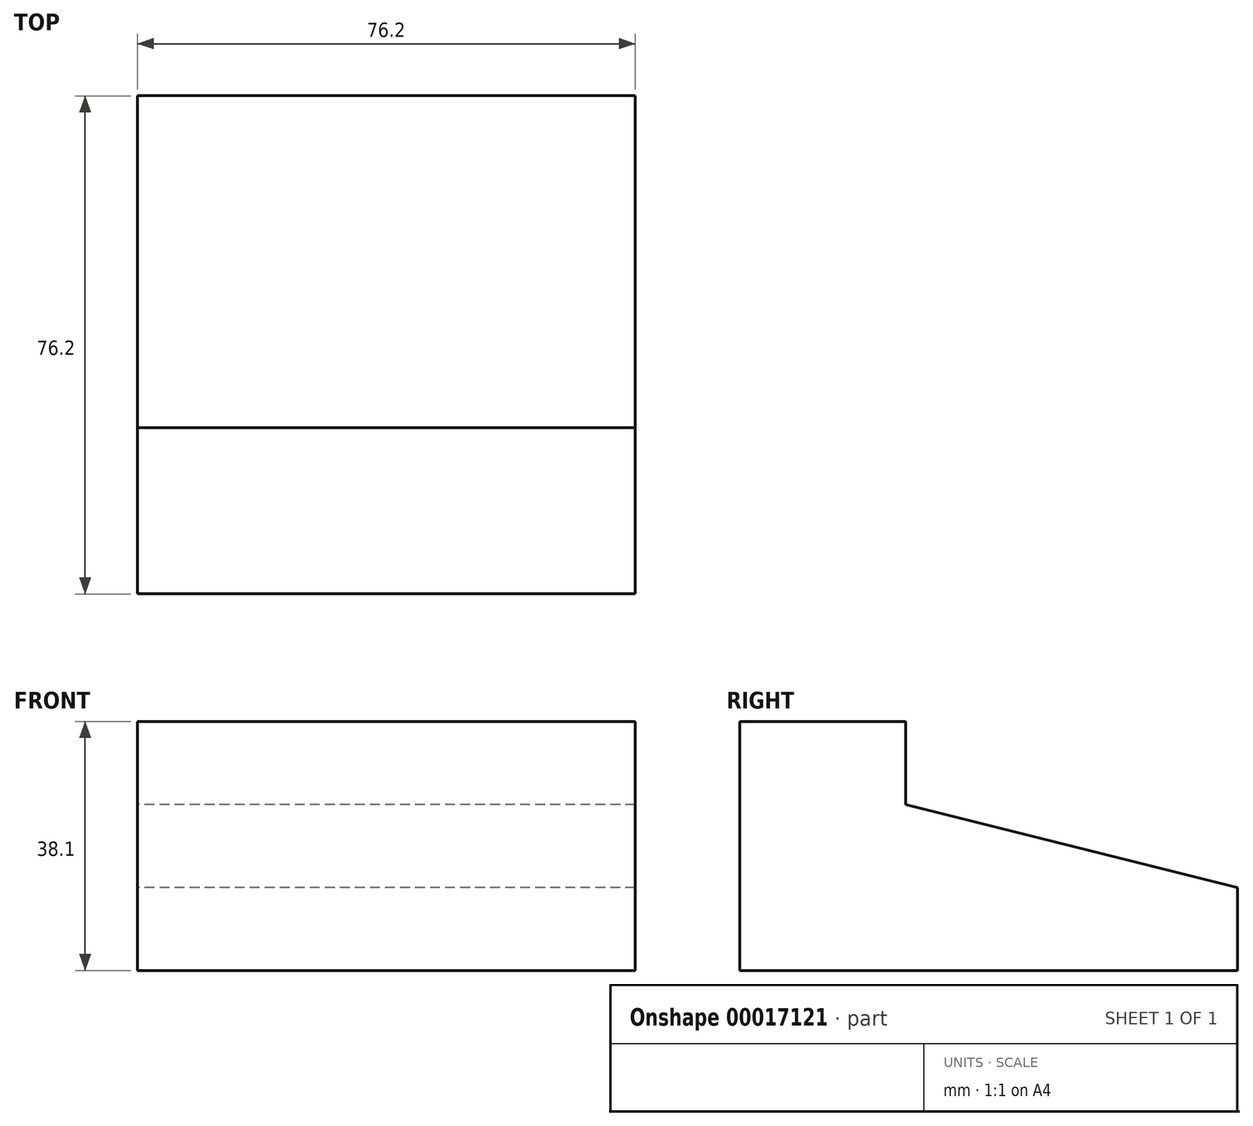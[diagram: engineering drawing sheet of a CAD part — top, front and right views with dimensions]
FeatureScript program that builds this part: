
annotation { "Feature Type Name" : "Feature", "Feature Type Description" : "" }
export const myFeature = defineFeature(function(context is Context, id is Id, definition is map)
    precondition{}
    {
        {
            var Q0;
            Q0=qCreatedBy(makeId("Right.planeOp"),FACE);
            var sketch = newSketch(context, id + "F0", { "sketchPlane" : qUnion([Q0])});
            skLineSegment(sketch, "E0", {"start": v(-41.72, 32.47) * mm, "end": v(-16.32, 32.47) * mm});
            skLineSegment(sketch, "E1", {"start": v(-16.32, 32.47) * mm, "end": v(-16.32, 19.77) * mm});
            skLineSegment(sketch, "E2", {"start": v(-16.32, 19.77) * mm, "end": v(34.48, 7.07) * mm});
            skLineSegment(sketch, "E3", {"start": v(34.48, 7.07) * mm, "end": v(34.48, -5.63) * mm});
            skLineSegment(sketch, "E4", {"start": v(34.48, -5.63) * mm, "end": v(-41.72, -5.63) * mm});
            skLineSegment(sketch, "E5", {"start": v(-41.72, 32.47) * mm, "end": v(-41.72, -5.63) * mm});
            skSolve(sketch);
        }
        {
            var Q0;
            Q0 = qSketchRegion(id + "F0", true);
            extrude(context, id + "F1", {"entities" : qUnion([Q0]), "depth" : 76.2 * mm});
        }
    });
